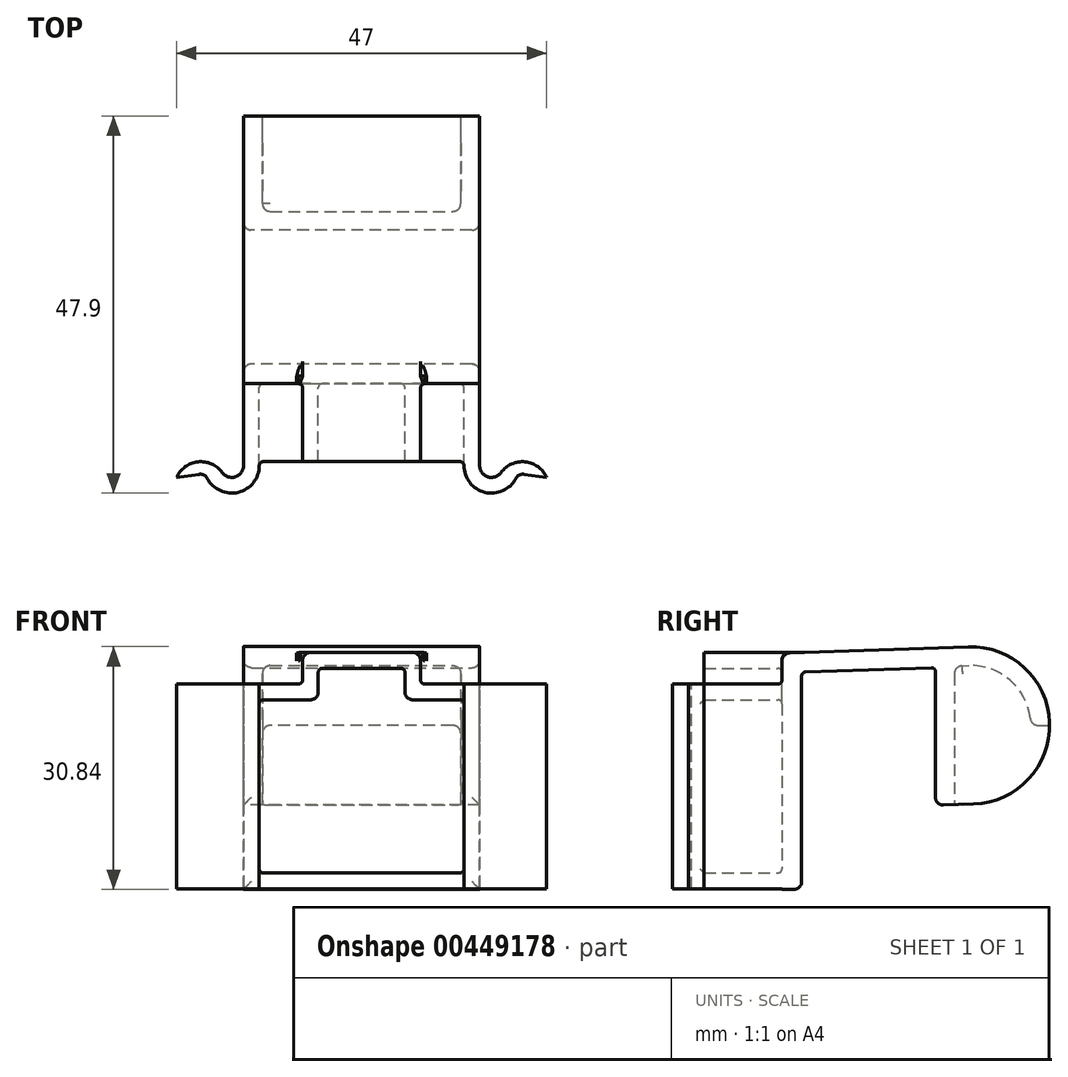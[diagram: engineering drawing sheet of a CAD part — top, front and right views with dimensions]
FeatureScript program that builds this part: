
annotation { "Feature Type Name" : "Feature", "Feature Type Description" : "" }
export const myFeature = defineFeature(function(context is Context, id is Id, definition is map)
    precondition{}
    {
        {
            var Q0;
            Q0=qCreatedBy(makeId("Right.planeOp"),FACE);
            var sketch = newSketch(context, id + "F0", { "sketchPlane" : qUnion([Q0])});
            skLineSegment(sketch, "E0", {"start": v(0, 0) * mm, "end": v(0, -27.59) * mm});
            skLineSegment(sketch, "E1", {"start": v(0, -27.59) * mm, "end": v(-2.5, -27.59) * mm});
            skLineSegment(sketch, "E2", {"start": v(-2.5, -27.59) * mm, "end": v(-2.5, 2.41) * mm});
            skLineSegment(sketch, "E3", {"start": v(-2.5, 2.41) * mm, "end": v(21.15, 3.24) * mm});
            skLineSegment(sketch, "E4", {"start": v(0, 0) * mm, "end": v(17, 0.6) * mm});
            skLineSegment(sketch, "E5", {"start": v(17, 0.6) * mm, "end": v(17, -16.92) * mm});
            skLineSegment(sketch, "E6", {"start": v(17, -16.92) * mm, "end": v(21.85, -16.75) * mm});
            skArc(sketch, "E7", {"start": v(21.85, -16.75) * mm, "mid": v(31.5, -6.4) * mm, "end": v(21.15, 3.24) * mm});
            skSolve(sketch);
        }
        {
            var Q0;
            Q0 = qSketchRegion(id + "F0", true);
            extrude(context, id + "F1", {"entities" : qUnion([Q0]), "endBound" : BoundingType.SYMMETRIC, "depth" : 30 * mm});
        }
        {
            var Q0;
            Q0=qCreatedBy(makeId("Front.planeOp"),FACE);
            var sketch = newSketch(context, id + "F2", { "sketchPlane" : qUnion([Q0])});
            skLineSegment(sketch, "E8", {"start": v(-15, -27.5) * mm, "end": v(-15, -1.5) * mm});
            skLineSegment(sketch, "E9", {"start": v(-15, -1.5) * mm, "end": v(-7.5, -1.5) * mm});
            skLineSegment(sketch, "E10", {"start": v(-7.5, -1.5) * mm, "end": v(-7.5, 2.5) * mm});
            skLineSegment(sketch, "E11", {"start": v(-7.5, 2.5) * mm, "end": v(7.5, 2.5) * mm});
            skLineSegment(sketch, "E12", {"start": v(7.5, 2.5) * mm, "end": v(7.5, -1.5) * mm});
            skLineSegment(sketch, "E13", {"start": v(7.5, -1.5) * mm, "end": v(15, -1.5) * mm});
            skLineSegment(sketch, "E14", {"start": v(15, -1.5) * mm, "end": v(15, -27.5) * mm});
            skLineSegment(sketch, "E15", {"start": v(15, -27.5) * mm, "end": v(-15, -27.5) * mm});
            skLineSegment(sketch, "E16.0", {"start": v(13, -25.5) * mm, "end": v(-13, -25.5) * mm});
            skLineSegment(sketch, "E16.1", {"start": v(13, -3.5) * mm, "end": v(13, -25.5) * mm});
            skLineSegment(sketch, "E16.2", {"start": v(-13, -25.5) * mm, "end": v(-13, -3.5) * mm});
            skLineSegment(sketch, "E16.3", {"start": v(5.5, -3.5) * mm, "end": v(13, -3.5) * mm});
            skLineSegment(sketch, "E16.4", {"start": v(-13, -3.5) * mm, "end": v(-5.5, -3.5) * mm});
            skLineSegment(sketch, "E16.5", {"start": v(-5.5, -3.5) * mm, "end": v(-5.5, 0.5) * mm});
            skLineSegment(sketch, "E16.6", {"start": v(-5.5, 0.5) * mm, "end": v(5.5, 0.5) * mm});
            skLineSegment(sketch, "E16.7", {"start": v(5.5, 0.5) * mm, "end": v(5.5, -3.5) * mm});
            skSolve(sketch);
        }
        {
            var Q0;
            Q0 = qSketchRegion(id + "F2", true);
            extrude(context, id + "F3", {"entities" : qUnion([Q0]), "operationType" : NewBodyOperationType.ADD, "depth" : 12.4 * mm});
        }
        {
            var Q0;
            Q0=qCreatedBy(makeId("Top.planeOp"),FACE);
            var sketch = newSketch(context, id + "F4", { "sketchPlane" : qUnion([Q0])});
            skLineSegment(sketch, "E17", {"start": v(-15, -12.9) * mm, "end": v(-15, -10.9) * mm});
            skArc(sketch, "E18", {"start": v(-17.71, -13.78) * mm, "mid": v(-16.04, -14.33) * mm, "end": v(-15, -12.9) * mm});
            skArc(sketch, "E19", {"start": v(-17.71, -13.78) * mm, "mid": v(-20.78, -12.42) * mm, "end": v(-23.5, -14.4) * mm});
            skLineSegment(sketch, "E20.0", {"start": v(-13, -12.9) * mm, "end": v(-13, -10.9) * mm});
            skArc(sketch, "E20.1", {"start": v(-19.85, -13.9) * mm, "mid": v(-16, -16.36) * mm, "end": v(-13, -12.9) * mm});
            skLineSegment(sketch, "E21", {"start": v(-19.85, -13.9) * mm, "end": v(-23.5, -14.4) * mm});
            skLineSegment(sketch, "E22", {"start": v(-13, -10.9) * mm, "end": v(-15, -10.9) * mm});
            skLineSegment(sketch, "E23.MirrorCS", {"start": v(13, -10.9) * mm, "end": v(15, -10.9) * mm});
            skLineSegment(sketch, "E24.MirrorCS", {"start": v(15, -12.9) * mm, "end": v(15, -10.9) * mm});
            skLineSegment(sketch, "E25.MirrorCS", {"start": v(13, -12.9) * mm, "end": v(13, -10.9) * mm});
            skArc(sketch, "E26.MirrorCS", {"start": v(19.85, -13.9) * mm, "mid": v(16, -16.36) * mm, "end": v(13, -12.9) * mm});
            skArc(sketch, "E27.MirrorCS", {"start": v(17.71, -13.78) * mm, "mid": v(16.04, -14.33) * mm, "end": v(15, -12.9) * mm});
            skArc(sketch, "E28.MirrorCS", {"start": v(17.71, -13.78) * mm, "mid": v(20.78, -12.42) * mm, "end": v(23.5, -14.4) * mm});
            skLineSegment(sketch, "E29.MirrorCS", {"start": v(19.85, -13.9) * mm, "end": v(23.5, -14.4) * mm});
            skSolve(sketch);
        }
        {
            var Q0;
            Q0 = qSketchRegion(id + "F4", true);
            extrude(context, id + "F5", {"entities" : qUnion([Q0]), "operationType" : NewBodyOperationType.ADD, "oppositeDirection" : true, "depth" : (30 - 2.5) * mm, "hasSecondDirection" : true, "secondDirectionOppositeDirection" : true, "secondDirectionDepth" : (4 - 2.5) * mm});
        }
        {
            var Q0;
            Q0=qCreatedBy(makeId("Right.planeOp"),FACE);
            var sketch = newSketch(context, id + "F6", { "sketchPlane" : qUnion([Q0])});
            skArc(sketch, "E30.0", {"start": v(29.1, -6.75) * mm, "mid": v(26.78, -1.29) * mm, "end": v(21.23, 0.84) * mm});
            skLineSegment(sketch, "E31.0", {"start": v(19.4, 0.78) * mm, "end": v(19.4, -22.57) * mm});
            skLineSegment(sketch, "E32.0", {"start": v(19.4, 0.78) * mm, "end": v(21.23, 0.84) * mm});
            skLineSegment(sketch, "E33", {"start": v(29.1, -6.75) * mm, "end": v(39.36, -6.75) * mm});
            skLineSegment(sketch, "E34", {"start": v(19.4, -22.57) * mm, "end": v(39.9, -22.57) * mm});
            skLineSegment(sketch, "E35", {"start": v(39.9, -22.57) * mm, "end": v(39.36, -6.75) * mm});
            skSolve(sketch);
        }
        {
            var Q0;
            Q0 = qSketchRegion(id + "F6", true);
            extrude(context, id + "F7", {"entities" : qUnion([Q0]), "operationType" : NewBodyOperationType.REMOVE, "oppositeDirection" : true, "depth" : (15 - 2.4) * mm, "hasSecondDirection" : true, "secondDirectionOppositeDirection" : false, "secondDirectionDepth" : (15 - 2.4) * mm});
        }
        {
            var Q0;
            Q0=makeQuery(id+"F3.boolean.opBoolean","INTERSECT",EDGE,{"derivedFrom":[makeQuery(id+"F1.opExtrude","SWEPT_FACE",FACE,{"disambiguationData":[OSD([sQuery(id+"F0.wireOp",EDGE,"E3")])]}),makeQuery(id+"F3.opExtrude","SWEPT_FACE",FACE,{"disambiguationData":[OSD([sQuery(id+"F2.wireOp",EDGE,"E11")])]})]});
            fillet(context, id + "F8", {"entities" : qUnion([Q0]), "radius" : 20 * mm, "tangentPropagation" : true, "allowEdgeOverflow" : false});
        }
        {
            var Q0;
            Q0=makeQuery(id+"F1.opExtrude","SWEPT_EDGE",EDGE,{"disambiguationData":[OSD([sQuery(id+"F0.wireOp",EDGE,"E0"),sQuery(id+"F0.wireOp",EDGE,"E4")])]});
            var Q1;
            Q1=makeQuery(id+"F1.opExtrude","SWEPT_EDGE",EDGE,{"disambiguationData":[OSD([sQuery(id+"F0.wireOp",EDGE,"E4"),sQuery(id+"F0.wireOp",EDGE,"E5")])]});
            fillet(context, id + "F9", {"entities" : qUnion([Q0, Q1]), "radius" : .5 * mm, "tangentPropagation" : true, "allowEdgeOverflow" : false});
        }
        {
            var Q0;
            Q0=makeQuery(id+"F1.opExtrude","CAP_EDGE",EDGE,{"disambiguationData":[OSD([sQuery(id+"F0.wireOp",EDGE,"E0")])],"isStart":true});
            var Q1;
            Q1=makeQuery(id+"F1.opExtrude","CAP_EDGE",EDGE,{"disambiguationData":[OSD([sQuery(id+"F0.wireOp",EDGE,"E0")])],"isStart":false});
            fillet(context, id + "F10", {"entities" : qUnion([Q0, Q1]), "radius" : 1 * mm, "tangentPropagation" : true, "allowEdgeOverflow" : false});
        }
        {
            var Q0;
            Q0=makeQuery(id+"F7.boolean.opBoolean","COPY",EDGE,{"derivedFrom":makeQuery(id+"F7.opExtrude","SWEPT_EDGE",EDGE,{"disambiguationData":[OSD([sQuery(id+"F6.wireOp",EDGE,"E31.0"),sQuery(id+"F6.wireOp",EDGE,"E32.0")])]})});
            var Q1;
            Q1=makeQuery(id+"F7.boolean.opBoolean","COPY",EDGE,{"derivedFrom":makeQuery(id+"F7.opExtrude","SWEPT_EDGE",EDGE,{"disambiguationData":[OSD([sQuery(id+"F6.wireOp",EDGE,"E30.0"),sQuery(id+"F6.wireOp",EDGE,"E33")])]})});
            fillet(context, id + "F11", {"entities" : qUnion([Q0, Q1]), "radius" : 1 * mm, "tangentPropagation" : true, "allowEdgeOverflow" : false});
        }
        {
            var Q0;
            Q0=makeQuery(id+"F7.boolean.opBoolean","COPY",EDGE,{"derivedFrom":makeQuery(id+"F7.opExtrude","CAP_EDGE",EDGE,{"disambiguationData":[OSD([sQuery(id+"F6.wireOp",EDGE,"E31.0")])],"isStart":true})});
            var Q1;
            Q1=makeQuery(id+"F7.boolean.opBoolean","COPY",EDGE,{"derivedFrom":makeQuery(id+"F7.opExtrude","CAP_EDGE",EDGE,{"disambiguationData":[OSD([sQuery(id+"F6.wireOp",EDGE,"E31.0")])],"isStart":false})});
            fillet(context, id + "F12", {"entities" : qUnion([Q0, Q1]), "radius" : 1 * mm, "tangentPropagation" : true, "allowEdgeOverflow" : false});
        }
        {
            var Q0;
            Q0=makeQuery(id+"F3.boolean.opBoolean","INTERSECT",EDGE,{"derivedFrom":[makeQuery(id+"F1.opExtrude","SWEPT_FACE",FACE,{"disambiguationData":[OSD([sQuery(id+"F0.wireOp",EDGE,"E3")])]}),makeQuery(id+"F3.opExtrude","SWEPT_FACE",FACE,{"disambiguationData":[OSD([sQuery(id+"F2.wireOp",EDGE,"E12")])]})]});
            var Q1;
            Q1=makeQuery(id+"F3.boolean.opBoolean","INTERSECT",EDGE,{"derivedFrom":[makeQuery(id+"F1.opExtrude","SWEPT_FACE",FACE,{"disambiguationData":[OSD([sQuery(id+"F0.wireOp",EDGE,"E3")])]}),makeQuery(id+"F3.opExtrude","SWEPT_FACE",FACE,{"disambiguationData":[OSD([sQuery(id+"F2.wireOp",EDGE,"E10")])]})]});
            fillet(context, id + "F13", {"entities" : qUnion([Q0, Q1]), "radius" : 5 * mm, "tangentPropagation" : true, "allowEdgeOverflow" : false});
        }
        {
            var Q0;
            Q0=makeQuery(id+"F3.boolean.opBoolean","INTERSECT",EDGE,{"derivedFrom":[makeQuery(id+"F1.opExtrude","SWEPT_FACE",FACE,{"disambiguationData":[OSD([sQuery(id+"F0.wireOp",EDGE,"E2")])]}),makeQuery(id+"F3.opExtrude","SWEPT_FACE",FACE,{"disambiguationData":[OSD([sQuery(id+"F2.wireOp",EDGE,"E10")])]})]});
            var Q1;
            Q1=makeQuery(id+"F3.boolean.opBoolean","INTERSECT",EDGE,{"derivedFrom":[makeQuery(id+"F1.opExtrude","SWEPT_FACE",FACE,{"disambiguationData":[OSD([sQuery(id+"F0.wireOp",EDGE,"E2")])]}),makeQuery(id+"F3.opExtrude","SWEPT_FACE",FACE,{"disambiguationData":[OSD([sQuery(id+"F2.wireOp",EDGE,"E12")])]})]});
            fillet(context, id + "F14", {"entities" : qUnion([Q0, Q1]), "radius" : 0.5 * mm, "tangentPropagation" : true, "allowEdgeOverflow" : false});
        }
        {
            var Q0;
            Q0=makeQuery(id+"F3.opExtrude","SWEPT_EDGE",EDGE,{"disambiguationData":[OSD([sQuery(id+"F2.wireOp",EDGE,"E12"),sQuery(id+"F2.wireOp",EDGE,"E13")])]});
            var Q1;
            Q1=makeQuery(id+"F3.opExtrude","SWEPT_EDGE",EDGE,{"disambiguationData":[OSD([sQuery(id+"F2.wireOp",EDGE,"E9"),sQuery(id+"F2.wireOp",EDGE,"E10")])]});
            fillet(context, id + "F15", {"entities" : qUnion([Q0, Q1]), "radius" : .5 * mm, "tangentPropagation" : true, "allowEdgeOverflow" : false});
        }
        {
            var Q0;
            Q0=makeQuery(id+"F3.opExtrude","SWEPT_EDGE",EDGE,{"disambiguationData":[OSD([sQuery(id+"F2.wireOp",EDGE,"E16.5"),sQuery(id+"F2.wireOp",EDGE,"E16.6")])]});
            var Q1;
            Q1=makeQuery(id+"F3.opExtrude","SWEPT_EDGE",EDGE,{"disambiguationData":[OSD([sQuery(id+"F2.wireOp",EDGE,"E16.2"),sQuery(id+"F2.wireOp",EDGE,"E16.4")])]});
            var Q2;
            Q2=makeQuery(id+"F3.opExtrude","SWEPT_EDGE",EDGE,{"disambiguationData":[OSD([sQuery(id+"F2.wireOp",EDGE,"E16.0"),sQuery(id+"F2.wireOp",EDGE,"E16.2")])]});
            var Q3;
            Q3=makeQuery(id+"F3.opExtrude","SWEPT_EDGE",EDGE,{"disambiguationData":[OSD([sQuery(id+"F2.wireOp",EDGE,"E16.0"),sQuery(id+"F2.wireOp",EDGE,"E16.1")])]});
            var Q4;
            Q4=makeQuery(id+"F3.opExtrude","SWEPT_EDGE",EDGE,{"disambiguationData":[OSD([sQuery(id+"F2.wireOp",EDGE,"E16.1"),sQuery(id+"F2.wireOp",EDGE,"E16.3")])]});
            var Q5;
            Q5=makeQuery(id+"F3.opExtrude","SWEPT_EDGE",EDGE,{"disambiguationData":[OSD([sQuery(id+"F2.wireOp",EDGE,"E16.6"),sQuery(id+"F2.wireOp",EDGE,"E16.7")])]});
            fillet(context, id + "F16", {"entities" : qUnion([Q0, Q1, Q2, Q3, Q4, Q5]), "radius" : .5 * mm, "tangentPropagation" : true, "allowEdgeOverflow" : false});
        }
        {
            var Q0;
            Q0=makeQuery(id+"F3.opExtrude","SWEPT_EDGE",EDGE,{"disambiguationData":[OSD([sQuery(id+"F2.wireOp",EDGE,"E16.3"),sQuery(id+"F2.wireOp",EDGE,"E16.7")])]});
            var Q1;
            Q1=makeQuery(id+"F3.opExtrude","SWEPT_EDGE",EDGE,{"disambiguationData":[OSD([sQuery(id+"F2.wireOp",EDGE,"E16.4"),sQuery(id+"F2.wireOp",EDGE,"E16.5")])]});
            fillet(context, id + "F17", {"entities" : qUnion([Q0, Q1]), "radius" : 1 * mm, "tangentPropagation" : true, "allowEdgeOverflow" : false});
        }
        {
            var Q0;
            Q0=makeQuery(id+"F3.boolean.opBoolean","INTERSECT",EDGE,{"derivedFrom":[makeQuery(id+"F1.opExtrude","SWEPT_FACE",FACE,{"disambiguationData":[OSD([sQuery(id+"F0.wireOp",EDGE,"E2")])]}),makeQuery(id+"F3.opExtrude","SWEPT_FACE",FACE,{"disambiguationData":[OSD([sQuery(id+"F2.wireOp",EDGE,"E16.2")])]})]});
            fillet(context, id + "F18", {"entities" : qUnion([Q0]), "radius" : .5 * mm, "tangentPropagation" : true, "allowEdgeOverflow" : false});
        }
        {
            var Q0;
            Q0=makeQuery(id+"F5.opExtrude","SWEPT_EDGE",EDGE,{"disambiguationData":[OSD([sQuery(id+"F4.wireOp",EDGE,"E26.MirrorCS"),sQuery(id+"F4.wireOp",EDGE,"E29.MirrorCS")])]});
            var Q1;
            Q1=makeQuery(id+"F5.opExtrude","SWEPT_EDGE",EDGE,{"disambiguationData":[OSD([sQuery(id+"F4.wireOp",EDGE,"E20.1"),sQuery(id+"F4.wireOp",EDGE,"E21")])]});
            fillet(context, id + "F19", {"entities" : qUnion([Q0, Q1]), "radius" : 1 * mm, "tangentPropagation" : true, "allowEdgeOverflow" : false});
        }
        {
            var Q0;
            Q0=makeQuery(id+"F3.opExtrude","SWEPT_EDGE",EDGE,{"disambiguationData":[OSD([sQuery(id+"F2.wireOp",EDGE,"E11"),sQuery(id+"F2.wireOp",EDGE,"E12")])]});
            var Q1;
            {var subQ0=sQuery(id+"F0.wireOp",EDGE,"E3");var subQ1=sQuery(id+"F0.wireOp",EDGE,"E2");Q1=makeQuery(id+"F3.boolean.opBoolean","SPLIT",EDGE,{"disambiguationData":[TD([makeQuery(id+"F3.opExtrude","SWEPT_FACE",FACE,{"disambiguationData":[OSD([sQuery(id+"F2.wireOp",EDGE,"E12")])]})])],"derivedFrom":makeQuery(id+"F1.opExtrude","SWEPT_EDGE",EDGE,{"disambiguationData":[OSD([subQ1,subQ0])]})});}
            var Q2;
            Q2=makeQuery(id+"F3.opExtrude","SWEPT_EDGE",EDGE,{"disambiguationData":[OSD([sQuery(id+"F2.wireOp",EDGE,"E10"),sQuery(id+"F2.wireOp",EDGE,"E11")])]});
            var Q3;
            {var subQ0=sQuery(id+"F0.wireOp",EDGE,"E3");var subQ1=sQuery(id+"F0.wireOp",EDGE,"E2");Q3=makeQuery(id+"F3.boolean.opBoolean","SPLIT",EDGE,{"disambiguationData":[TD([makeQuery(id+"F3.opExtrude","SWEPT_FACE",FACE,{"disambiguationData":[OSD([sQuery(id+"F2.wireOp",EDGE,"E8")])]})])],"derivedFrom":makeQuery(id+"F1.opExtrude","SWEPT_EDGE",EDGE,{"disambiguationData":[OSD([subQ1,subQ0])]})});}
            fillet(context, id + "F20", {"entities" : qUnion([Q0, Q1, Q2, Q3]), "radius" : 1 * mm, "tangentPropagation" : true, "allowEdgeOverflow" : false});
        }
        {
            var Q0;
            Q0=makeQuery(id+"F5.boolean.opBoolean","INTERSECT",EDGE,{"disambiguationData":[OD(1.0)],"derivedFrom":[makeQuery(id+"F3.opExtrude","CAP_FACE",FACE,{"disambiguationData":[OSD([sQuery(id+"F2.wireOp",EDGE,"E8"),sQuery(id+"F2.wireOp",EDGE,"E9"),sQuery(id+"F2.wireOp",EDGE,"E10"),sQuery(id+"F2.wireOp",EDGE,"E11"),sQuery(id+"F2.wireOp",EDGE,"E12"),sQuery(id+"F2.wireOp",EDGE,"E13"),sQuery(id+"F2.wireOp",EDGE,"E14"),sQuery(id+"F2.wireOp",EDGE,"E15"),sQuery(id+"F2.wireOp",EDGE,"E16.0"),sQuery(id+"F2.wireOp",EDGE,"E16.1"),sQuery(id+"F2.wireOp",EDGE,"E16.2"),sQuery(id+"F2.wireOp",EDGE,"E16.3"),sQuery(id+"F2.wireOp",EDGE,"E16.4"),sQuery(id+"F2.wireOp",EDGE,"E16.5"),sQuery(id+"F2.wireOp",EDGE,"E16.6"),sQuery(id+"F2.wireOp",EDGE,"E16.7")])],"isStart":false}),makeQuery(id+"F5.opExtrude","SWEPT_FACE",FACE,{"disambiguationData":[OSD([sQuery(id+"F4.wireOp",EDGE,"E20.0")])]})]});
            var Q1;
            Q1=makeQuery(id+"F5.boolean.opBoolean","INTERSECT",EDGE,{"disambiguationData":[OD(1.0)],"derivedFrom":[makeQuery(id+"F3.opExtrude","CAP_FACE",FACE,{"disambiguationData":[OSD([sQuery(id+"F2.wireOp",EDGE,"E8"),sQuery(id+"F2.wireOp",EDGE,"E9"),sQuery(id+"F2.wireOp",EDGE,"E10"),sQuery(id+"F2.wireOp",EDGE,"E11"),sQuery(id+"F2.wireOp",EDGE,"E12"),sQuery(id+"F2.wireOp",EDGE,"E13"),sQuery(id+"F2.wireOp",EDGE,"E14"),sQuery(id+"F2.wireOp",EDGE,"E15"),sQuery(id+"F2.wireOp",EDGE,"E16.0"),sQuery(id+"F2.wireOp",EDGE,"E16.1"),sQuery(id+"F2.wireOp",EDGE,"E16.2"),sQuery(id+"F2.wireOp",EDGE,"E16.3"),sQuery(id+"F2.wireOp",EDGE,"E16.4"),sQuery(id+"F2.wireOp",EDGE,"E16.5"),sQuery(id+"F2.wireOp",EDGE,"E16.6"),sQuery(id+"F2.wireOp",EDGE,"E16.7")])],"isStart":false}),makeQuery(id+"F5.opExtrude","SWEPT_FACE",FACE,{"disambiguationData":[OSD([sQuery(id+"F4.wireOp",EDGE,"E25.MirrorCS")])]})]});
            var Q2;
            Q2=makeQuery(id+"F5.boolean.opBoolean","INTERSECT",EDGE,{"disambiguationData":[OD(0.0)],"derivedFrom":[makeQuery(id+"F3.opExtrude","CAP_FACE",FACE,{"disambiguationData":[OSD([sQuery(id+"F2.wireOp",EDGE,"E8"),sQuery(id+"F2.wireOp",EDGE,"E9"),sQuery(id+"F2.wireOp",EDGE,"E10"),sQuery(id+"F2.wireOp",EDGE,"E11"),sQuery(id+"F2.wireOp",EDGE,"E12"),sQuery(id+"F2.wireOp",EDGE,"E13"),sQuery(id+"F2.wireOp",EDGE,"E14"),sQuery(id+"F2.wireOp",EDGE,"E15"),sQuery(id+"F2.wireOp",EDGE,"E16.0"),sQuery(id+"F2.wireOp",EDGE,"E16.1"),sQuery(id+"F2.wireOp",EDGE,"E16.2"),sQuery(id+"F2.wireOp",EDGE,"E16.3"),sQuery(id+"F2.wireOp",EDGE,"E16.4"),sQuery(id+"F2.wireOp",EDGE,"E16.5"),sQuery(id+"F2.wireOp",EDGE,"E16.6"),sQuery(id+"F2.wireOp",EDGE,"E16.7")])],"isStart":false}),makeQuery(id+"F5.opExtrude","SWEPT_FACE",FACE,{"disambiguationData":[OSD([sQuery(id+"F4.wireOp",EDGE,"E25.MirrorCS")])]})]});
            var Q3;
            Q3=makeQuery(id+"F5.boolean.opBoolean","INTERSECT",EDGE,{"disambiguationData":[OD(0.0)],"derivedFrom":[makeQuery(id+"F3.opExtrude","CAP_FACE",FACE,{"disambiguationData":[OSD([sQuery(id+"F2.wireOp",EDGE,"E8"),sQuery(id+"F2.wireOp",EDGE,"E9"),sQuery(id+"F2.wireOp",EDGE,"E10"),sQuery(id+"F2.wireOp",EDGE,"E11"),sQuery(id+"F2.wireOp",EDGE,"E12"),sQuery(id+"F2.wireOp",EDGE,"E13"),sQuery(id+"F2.wireOp",EDGE,"E14"),sQuery(id+"F2.wireOp",EDGE,"E15"),sQuery(id+"F2.wireOp",EDGE,"E16.0"),sQuery(id+"F2.wireOp",EDGE,"E16.1"),sQuery(id+"F2.wireOp",EDGE,"E16.2"),sQuery(id+"F2.wireOp",EDGE,"E16.3"),sQuery(id+"F2.wireOp",EDGE,"E16.4"),sQuery(id+"F2.wireOp",EDGE,"E16.5"),sQuery(id+"F2.wireOp",EDGE,"E16.6"),sQuery(id+"F2.wireOp",EDGE,"E16.7")])],"isStart":false}),makeQuery(id+"F5.opExtrude","SWEPT_FACE",FACE,{"disambiguationData":[OSD([sQuery(id+"F4.wireOp",EDGE,"E20.0")])]})]});
            fillet(context, id + "F21", {"entities" : qUnion([Q0, Q1, Q2, Q3]), "radius" : .5 * mm, "tangentPropagation" : true, "allowEdgeOverflow" : false});
        }
        {
            var Q0;
            Q0=makeQuery(id+"F1.opExtrude","SWEPT_EDGE",EDGE,{"disambiguationData":[OSD([sQuery(id+"F0.wireOp",EDGE,"E0"),sQuery(id+"F0.wireOp",EDGE,"E1")])]});
            var Q1;
            Q1=makeQuery(id+"F1.opExtrude","SWEPT_EDGE",EDGE,{"disambiguationData":[OSD([sQuery(id+"F0.wireOp",EDGE,"E5"),sQuery(id+"F0.wireOp",EDGE,"E6")])]});
            fillet(context, id + "F22", {"entities" : qUnion([Q0, Q1]), "radius" : 1 * mm, "allowEdgeOverflow" : false});
        }
    });
